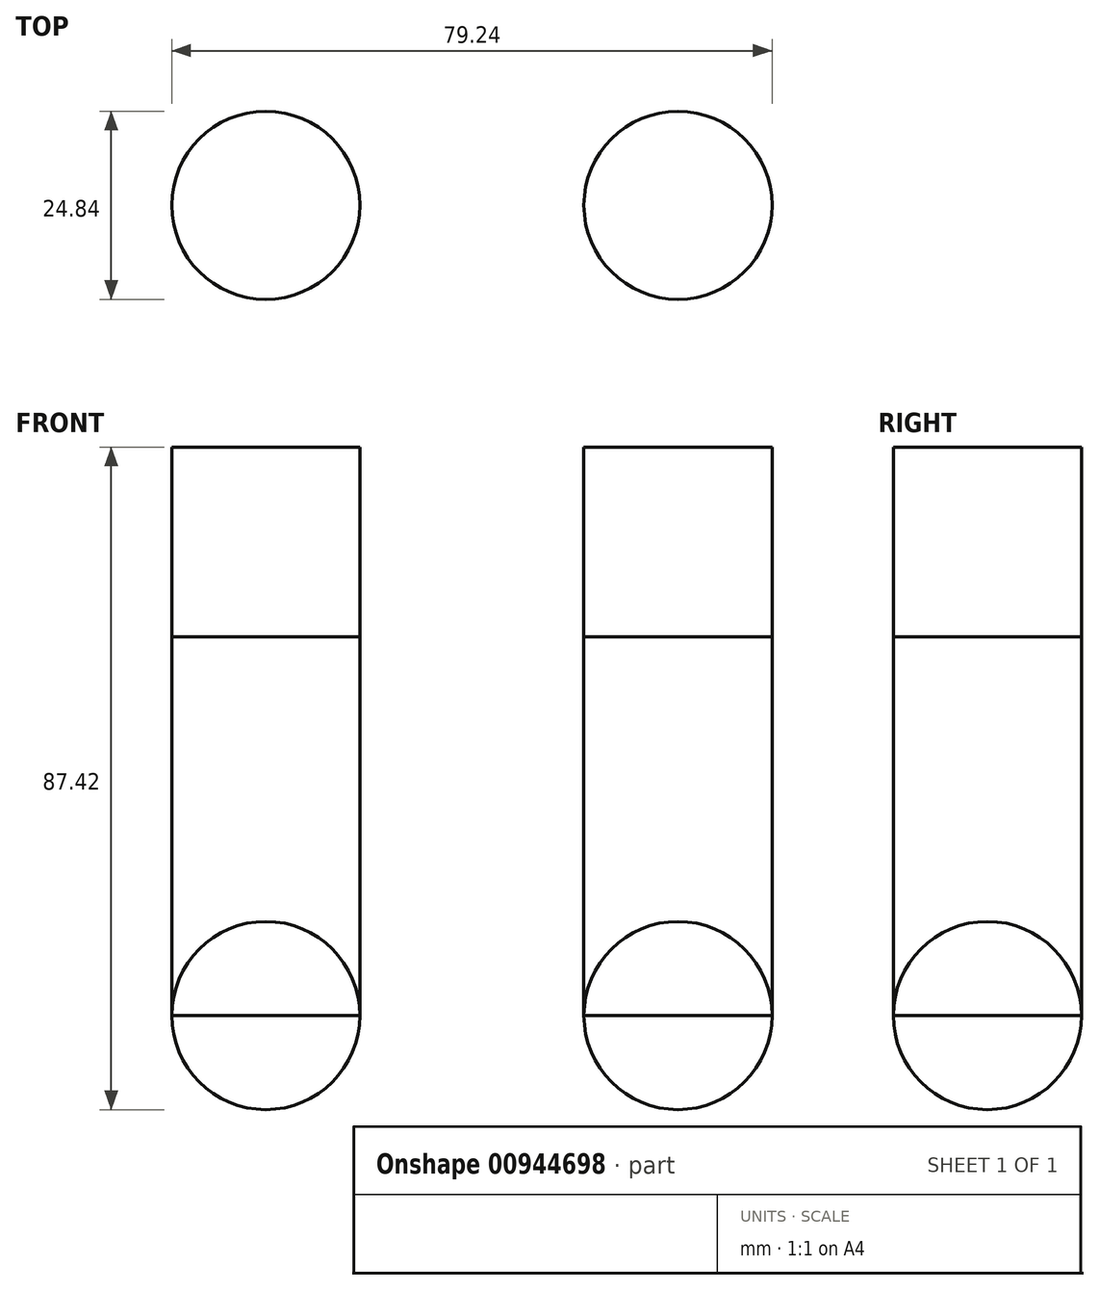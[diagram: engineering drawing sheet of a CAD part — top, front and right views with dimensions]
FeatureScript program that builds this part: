
annotation { "Feature Type Name" : "Feature", "Feature Type Description" : "" }
export const myFeature = defineFeature(function(context is Context, id is Id, definition is map)
    precondition{}
    {
        {
            var Q0;
            Q0=qCreatedBy(makeId("Top.planeOp"),FACE);
            var sketch = newSketch(context, id + "F0", { "sketchPlane" : qUnion([Q0])});
            skLineSegment(sketch, "E0", {"start": v(0, 0) * mm, "end": v(0, 35.7) * mm});
            skLineSegment(sketch, "E1", {"start": v(0, 0) * mm, "end": v(-27.2, 0) * mm});
            skLineSegment(sketch, "E2.MirrorCS", {"start": v(0, 0) * mm, "end": v(27.2, 0) * mm});
            skCircle(sketch, "E3", {"center": v(-27.2, 0) * mm, "radius": 12.42 * mm});
            skCircle(sketch, "E4.MirrorC", {"center": v(27.2, 0) * mm, "radius": 12.42 * mm});
            skLineSegment(sketch, "E5", {"start": v(27.2, 0) * mm, "end": v(39.62, 0) * mm});
            skLineSegment(sketch, "E6", {"start": v(-27.2, 0) * mm, "end": v(-39.62, 0) * mm});
            skSolve(sketch);
        }
        {
            var Q0;
            Q0 = qSketchRegion(id + "F0", true);
            extrude(context, id + "F1", {"entities" : qUnion([Q0]), "depth" : 50 * mm, "offsetDistance" : 25.4 * mm});
        }
        {
            var Q0;
            {var subQ0=sQuery(id+"F0.wireOp",EDGE,"E6");Q0=makeQuery(id+"F0.imprint","IMPRINT",FACE,{"disambiguationData":[TD([[makeQuery(id+"F0.imprint","IMPRINT",EDGE,{"derivedFrom":subQ0}),1.0]])]});}
            var Q1;
            {var subQ0=sQuery(id+"F0.wireOp",EDGE,"E5");Q1=makeQuery(id+"F0.imprint","IMPRINT",FACE,{"disambiguationData":[TD([[makeQuery(id+"F0.imprint","IMPRINT",EDGE,{"derivedFrom":subQ0}),-1.0]])]});}
            var Q2;
            Q2=sQuery(id+"F0.wireOp",EDGE,"E1");
            revolve(context, id + "F2", {"surfaceOperationType" : NewSurfaceOperationType.NEW, "entities" : qUnion([Q0, Q1]), "axis" : qUnion([Q2]), "revolveType" : RevolveType.FULL});
        }
        {
            var Q0;
            Q0=makeQuery(id+"F1.opExtrude","CAP_FACE",FACE,{"disambiguationData":[OSD([sQuery(id+"F0.wireOp",EDGE,"E4.MirrorC")])],"isStart":false});
            var Q1;
            Q1=makeQuery(id+"F1.opExtrude","CAP_FACE",FACE,{"disambiguationData":[OSD([sQuery(id+"F0.wireOp",EDGE,"E3")])],"isStart":false});
            extrude(context, id + "F3", {"entities" : qUnion([Q0, Q1]), "depth" : 25 * mm, "offsetDistance" : 25.4 * mm});
        }
    });
